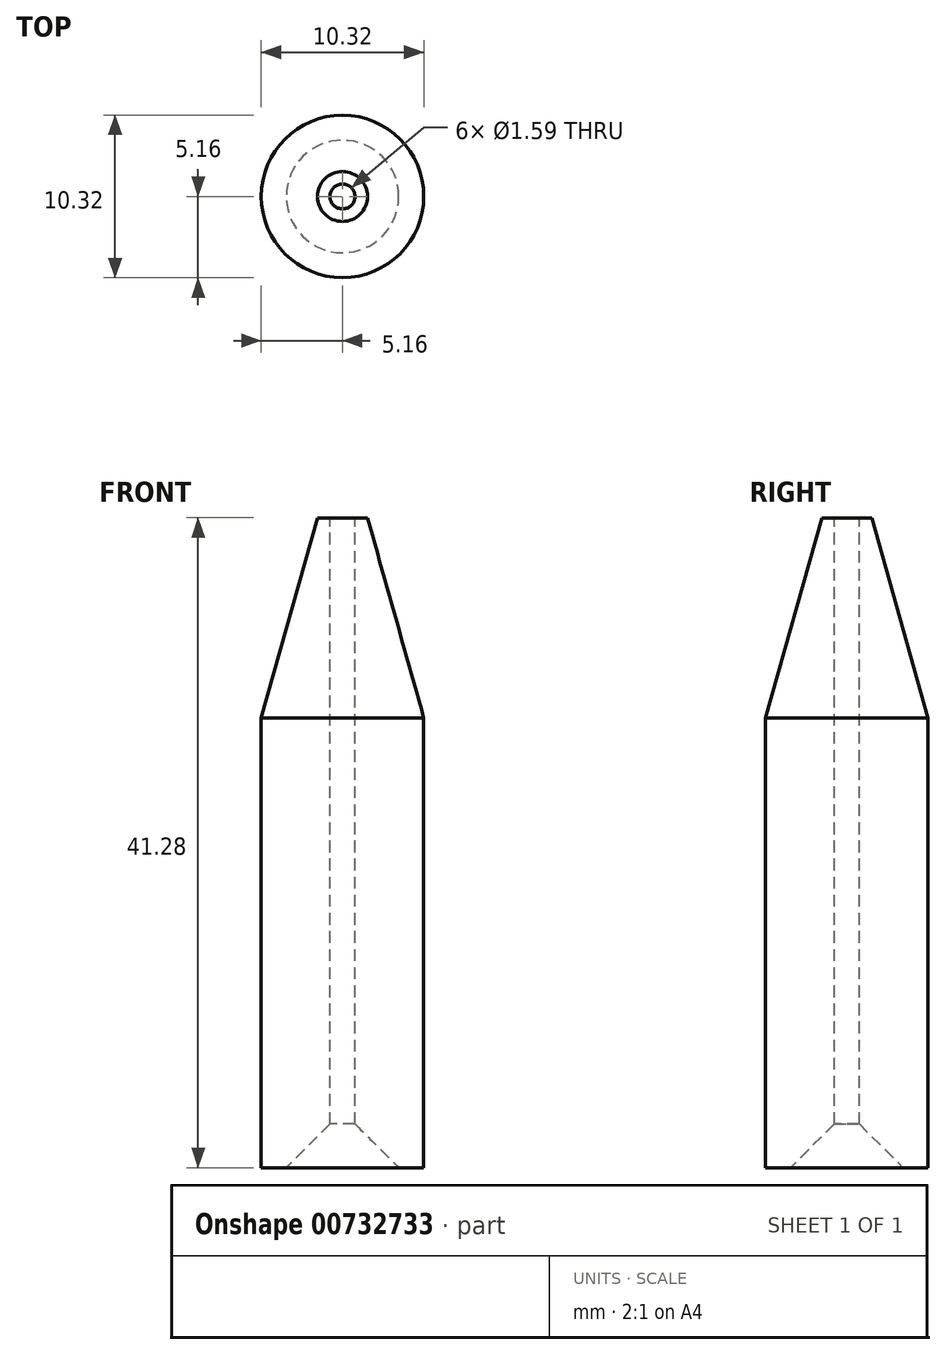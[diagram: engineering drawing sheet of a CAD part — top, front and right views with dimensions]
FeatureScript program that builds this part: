
annotation { "Feature Type Name" : "Feature", "Feature Type Description" : "" }
export const myFeature = defineFeature(function(context is Context, id is Id, definition is map)
    precondition{}
    {
        {
            var Q0;
            Q0=qCreatedBy(makeId("Front.planeOp"),FACE);
            var sketch = newSketch(context, id + "F0", { "sketchPlane" : qUnion([Q0])});
            skLineSegment(sketch, "E0", {"start": v(0, 0) * mm, "end": v(5.16, 0) * mm, "construction": true});
            skLineSegment(sketch, "E1", {"start": v(5.16, 0) * mm, "end": v(5.16, 28.58) * mm});
            skLineSegment(sketch, "E2", {"start": v(0, 46.92) * mm, "end": v(0, 0) * mm, "construction": true});
            skLineSegment(sketch, "E3", {"start": v(5.16, 28.58) * mm, "end": v(0, 46.92) * mm, "construction": true});
            skLineSegment(sketch, "E4", {"start": v(5.16, 28.57) * mm, "end": v(1.59, 41.28) * mm});
            skLineSegment(sketch, "E5", {"start": v(1.59, 41.28) * mm, "end": v(0, 41.28) * mm});
            skLineSegment(sketch, "E6", {"start": v(0.8, 41.28) * mm, "end": v(0.8, 0) * mm});
            skLineSegment(sketch, "E7", {"start": v(0.8, 0) * mm, "end": v(5.16, 0) * mm});
            skLineSegment(sketch, "E8", {"start": v(0.8, 2.78) * mm, "end": v(3.57, 0) * mm});
            skSolve(sketch);
        }
        {
            var Q0;
            Q0=makeQuery(id+"F0.imprint","IMPRINT",FACE,{"disambiguationData":[TD([[makeQuery(id+"F0.imprint","IMPRINT",EDGE,{"derivedFrom":sQuery(id+"F0.wireOp",EDGE,"E1")}),1.0]])]});
            var Q1;
            Q1=sQuery(id+"F0.wireOp",EDGE,"E2");
            revolve(context, id + "F1", {"surfaceOperationType" : NewSurfaceOperationType.NEW, "entities" : qUnion([Q0]), "axis" : qUnion([Q1]), "revolveType" : RevolveType.FULL});
        }
    });
